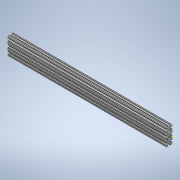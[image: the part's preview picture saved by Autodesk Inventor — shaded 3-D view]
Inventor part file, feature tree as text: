
AUTODESK INVENTOR PART (.ipt)
format: ipt  version: 2020 (Build 240168000, 168)  size: 378,880 bytes
history: native  units: in
note: dims shown in document units (in); Inventor stores cm internally (conversion verified against a paired STEP export)
features: sketch x2, extrude x1
ambient origin geometry x8: Origin, YZ Plane, XZ Plane, XY Plane, X Axis, Y Axis, Z Axis, Center Point
bodies: Solid1 (feature_tree)
feature tree (3):
  extrude  "Extrusion1"  [1 undecoded]
  sketch  "Sketch2"
  sketch  "Sketch1"  dims[d0=27.0in d1=0.0in]
note: 1 required parameter value undecoded (feature->parameter linkage not recoverable at this tier; creation-order binding heuristic only, values carry confidence <= 0.55)
